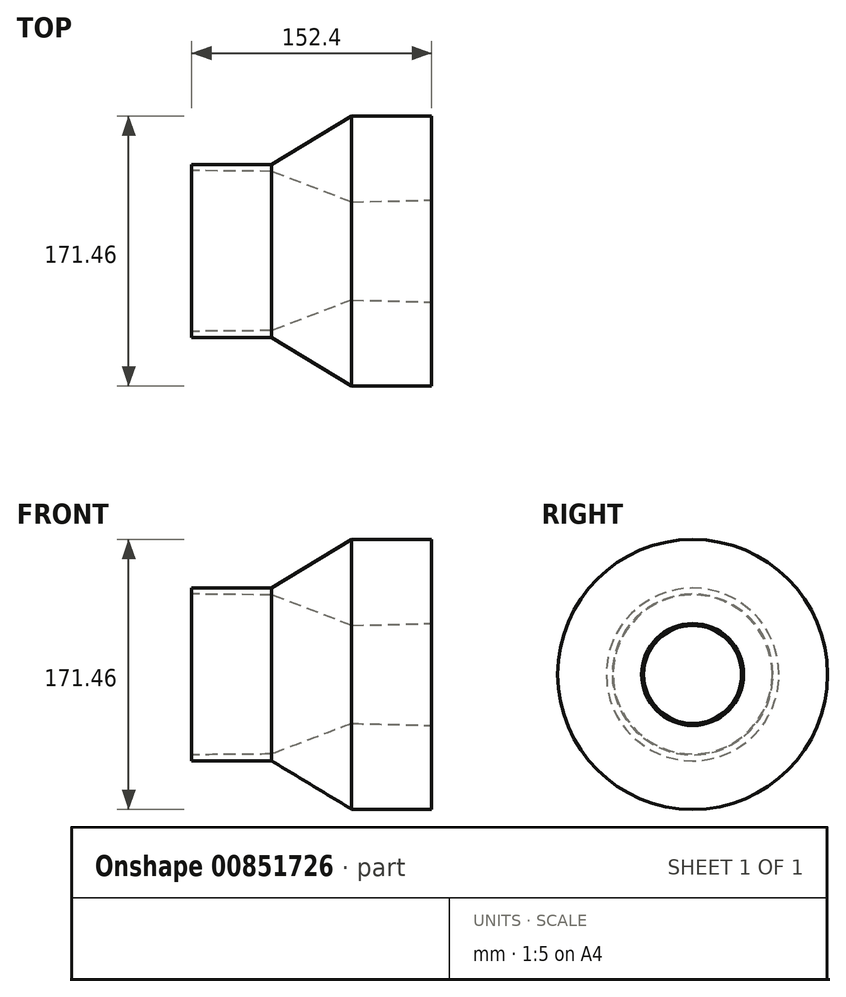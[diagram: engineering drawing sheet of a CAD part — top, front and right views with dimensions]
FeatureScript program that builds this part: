
annotation { "Feature Type Name" : "Feature", "Feature Type Description" : "" }
export const myFeature = defineFeature(function(context is Context, id is Id, definition is map)
    precondition{}
    {
        {
            var Q0;
            Q0=qCreatedBy(makeId("Front.planeOp"),FACE);
            var sketch = newSketch(context, id + "F0", { "sketchPlane" : qUnion([Q0])});
            skLineSegment(sketch, "E0", {"start": v(0, 0) * mm, "end": v(-90.9, 0) * mm, "construction": true});
            skLineSegment(sketch, "E1", {"start": v(0, 85.73) * mm, "end": v(50.8, 85.73) * mm});
            skLineSegment(sketch, "E2", {"start": v(50.8, 85.73) * mm, "end": v(50.8, 32.39) * mm});
            skLineSegment(sketch, "E3", {"start": v(50.8, 32.39) * mm, "end": v(0, 31.12) * mm});
            skLineSegment(sketch, "E4", {"start": v(0, 31.11) * mm, "end": v(-50.8, 50.55) * mm});
            skLineSegment(sketch, "E5", {"start": v(-50.8, 50.55) * mm, "end": v(-101.6, 51.05) * mm});
            skLineSegment(sketch, "E6", {"start": v(-101.6, 51.05) * mm, "end": v(-101.6, 54.86) * mm});
            skLineSegment(sketch, "E7", {"start": v(-101.6, 54.86) * mm, "end": v(-50.8, 54.86) * mm});
            skLineSegment(sketch, "E8", {"start": v(-50.8, 54.86) * mm, "end": v(0, 85.72) * mm});
            skPoint(sketch, "E9", {"position": v(25.4, 31.75) * mm});
            skPoint(sketch, "E10", {"position": v(-76.2, 50.8) * mm});
            skLineSegment(sketch, "E11", {"start": v(-50.8, 50.55) * mm, "end": v(-50.8, 54.86) * mm, "construction": true});
            skSolve(sketch);
        }
        {
            var Q0;
            Q0=qSketchRegion(id+"F0",true);
            var Q1;
            Q1=sQuery(id+"F0.wireOp",EDGE,"E0");
            revolve(context, id + "F1", {"surfaceOperationType" : NewSurfaceOperationType.NEW, "entities" : qUnion([Q0]), "axis" : qUnion([Q1]), "revolveType" : RevolveType.FULL});
        }
    });
